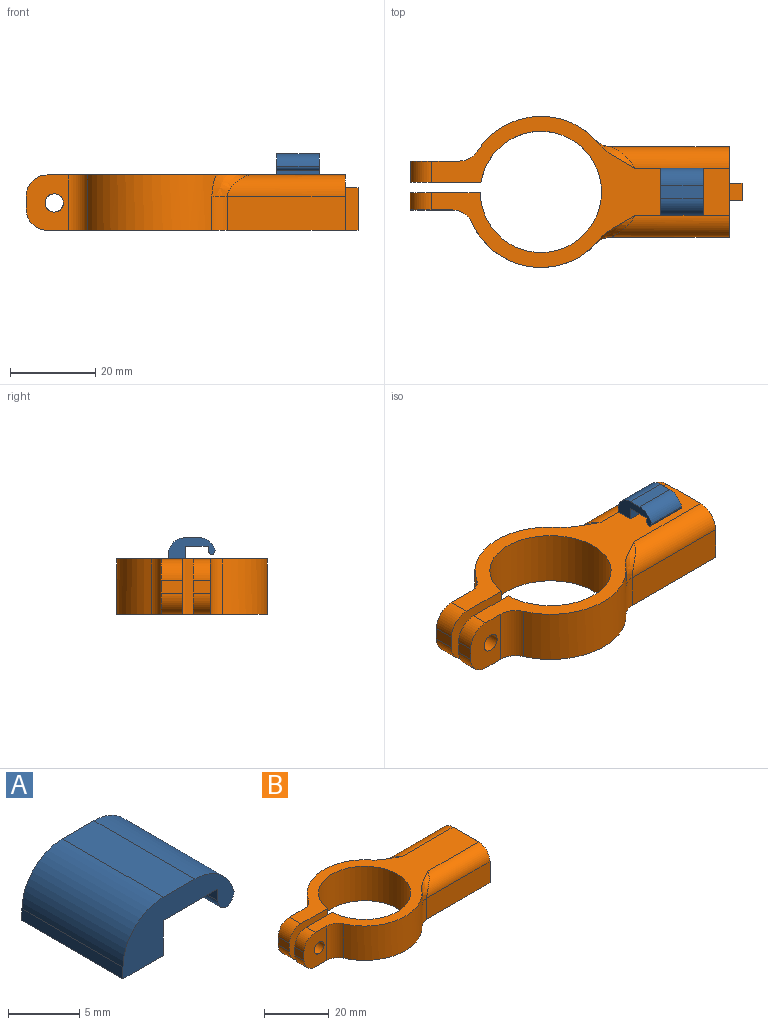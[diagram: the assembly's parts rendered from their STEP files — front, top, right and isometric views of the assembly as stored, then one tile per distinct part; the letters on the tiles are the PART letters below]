
ASSEMBLY  parts=2 mates=1
PART A: 12 faces, bbox 11x10x5 mm
  f0: plane 10x5.4mm, normal (0,0,-1), area 54mm2, adj f1,f3,f4,f7
  f1: plane 11x5mm, normal (0,1,0), area 30.3mm2, adj f0,f2,f4,f5,f6,f7,f8,f9
  f2: plane 10x1mm, normal (-1,0,0), area 10mm2, adj f1,f3,f6,f11
  f3: plane 11x5mm, normal (0,-1,0), area 30.3mm2, adj f0,f2,f4,f5,f6,f7,f8,f9
  f4: plane 10x3mm, normal (1,0,0), area 30mm2, adj f0,f1,f3,f6
  f5: plane 10x3.13mm, normal (0,0,1), area 31.3mm2, adj f1,f3,f10,f11
  f6: plane 10x4mm, normal (0,0,-1), area 40mm2, adj f1,f2,f3,f4
  f7: plane 10x1mm, normal (-1,0,0), area 10mm2, adj f0,f1,f3,f9
  f8: cylinder r=1mm len=10mm, axis (0,1,0), area 13.7mm2, adj f1,f3,f9,f10
  f9: cylinder r=1mm len=10mm, axis (0,-1,0), area 13.7mm2, adj f1,f3,f7,f8
  f10: cylinder r=4mm len=10mm, axis (0,1,0), area 52.7mm2, adj f1,f3,f5,f8
  f11: cylinder r=4mm len=10mm, axis (0,1,0), area 62.8mm2, adj f1,f2,f3,f5
PART B: 41 faces, bbox 80.3x37.8x20.3 mm
  f0: plane 21.17x13mm, normal (1,0,0), area 224.4mm2, adj f4,f5,f21,f22,f23,f24,f25,f29
  f1: cylinder r=17.75mm len=30.06mm, axis (0,0,-1), area 457.8mm2, adj f4,f5,f34,f39,f40
  f2: cylinder r=17.75mm len=28.79mm, axis (0,0,-1), area 422.9mm2, adj f4,f5,f31,f37,f38
  f3: cylinder r=14.25mm len=28.5mm, axis (0,0,-1), area 1131.3mm2, adj f4,f5,f6,f7
  f4: plane 72.3x37.8mm, normal (0,0,1), area 742.6mm2, adj f0,f1,f2,f3,f6,f7,f8,f18
  f5: plane 73x35.5mm, normal (0,0,-1), area 1020.1mm2, adj f0,f1,f2,f3,f6,f7,f8,f18
  f6: plane 16.54x13mm, normal (0,-1,0), area 189.7mm2, adj f3,f4,f5,f14,f16,f32,f33
  f7: plane 16.5x13mm, normal (0,1,0), area 189.3mm2, adj f3,f4,f5,f19,f20,f35,f36
  f8: plane 13x11.44mm, normal (0,1,0), area 82.6mm2, adj f4,f5,f9,f10,f11,f12,f13,f14
  f9: plane 4x3.4mm, normal (-0.87,0,0.5), area 15.7mm2, adj f8,f10,f15,f17
  f10: plane 4.62x3.4mm, normal (0,0,1), area 15.7mm2, adj f8,f9,f11,f17
  f11: plane 4x3.4mm, normal (0.87,0,0.5), area 15.7mm2, adj f8,f10,f12,f17
  f12: plane 4x3.4mm, normal (0.87,0,-0.5), area 15.7mm2, adj f8,f11,f13,f17
  f13: plane 4.62x3.4mm, normal (0,0,-1), area 15.7mm2, adj f8,f12,f15,f17
  f14: plane 5x3mm, normal (-1,0,0), area 15mm2, adj f6,f8,f32,f33
  f15: plane 4x3.4mm, normal (-0.87,0,-0.5), area 15.7mm2, adj f8,f9,f13,f17
  f16: cylinder r=2.15mm len=4.3mm, axis (0,-1,0), area 21.6mm2, adj f6,f17
  f17: plane 9.24x8mm, normal (0,1,0), area 40.9mm2, adj f9,f10,f11,f12,f13,f15,f16
  f18: plane 13x9.96mm, normal (0,-1,0), area 104.2mm2, adj f4,f5,f19,f20,f34,f35,f36
  f19: plane 4x3mm, normal (-1,0,0), area 12mm2, adj f7,f18,f35,f36
  f20: cylinder r=2.15mm len=4.3mm, axis (0,1,0), area 54mm2, adj f7,f18
  f21: plane 27.68x8mm, normal (0,1,0), area 221.4mm2, adj f0,f5,f30,f37
  f22: plane 27.68x8mm, normal (0,-1,0), area 221.4mm2, adj f0,f5,f29,f39
  f23: plane 10x3mm, normal (0,1,0), area 30mm2, adj f0,f5,f24,f26
  f24: plane 4x3mm, normal (0,0,1), area 12mm2, adj f0,f23,f25,f26
  f25: plane 10x3mm, normal (0,-1,0), area 30mm2, adj f0,f5,f24,f26
  f26: plane 10x4mm, normal (1,0,0), area 36.9mm2, adj f5,f23,f24,f25,f28
  f27: plane 2x2mm, normal (1,0,0), area 3.1mm2, adj f28
  f28: cylinder r=1mm len=7mm, axis (1,0,0), area 44mm2, adj f26,f27
  f29: cylinder r=5mm len=27.68mm, axis (1,0,0), area 195.8mm2, adj f0,f4,f22,f40
  f30: cylinder r=5mm len=27.68mm, axis (-1,0,0), area 195.8mm2, adj f0,f4,f21,f38
  f31: cylinder r=5mm len=13mm, axis (0,0,-1), area 65.1mm2, adj f2,f4,f5,f8
  f32: cylinder r=5mm len=5mm, axis (0,-1,0), area 39.3mm2, adj f4,f6,f8,f14
  f33: cylinder r=5mm len=5mm, axis (0,1,0), area 39.3mm2, adj f5,f6,f8,f14
  f34: cylinder r=5mm len=13mm, axis (0,0,-1), area 74.9mm2, adj f1,f4,f5,f18
  f35: cylinder r=5mm len=5mm, axis (0,-1,0), area 31.4mm2, adj f4,f7,f18,f19
  f36: cylinder r=5mm len=5mm, axis (0,1,0), area 31.4mm2, adj f5,f7,f18,f19
  f37: cylinder r=5mm len=8mm, axis (0,0,-1), area 32.6mm2, adj f2,f5,f21,f38
  f38: bspline ~10.49x9.44mm, area 39.1mm2, adj f2,f4,f30,f37
  f39: cylinder r=5mm len=8mm, axis (0,0,-1), area 32.6mm2, adj f1,f5,f22,f40
  f40: bspline ~10.49x9.44mm, area 39.1mm2, adj f1,f4,f29,f39
PLACE A rot(axis=(0,0,-1),90deg) t=(30.88,7.87,9.08)mm
PLACE B t=(-7.27,2.28,-3.92)mm
MATE fastened A.f6 <-> B.f4  axis (0,0,-1) through (25.88,7.87,9.08)mm
